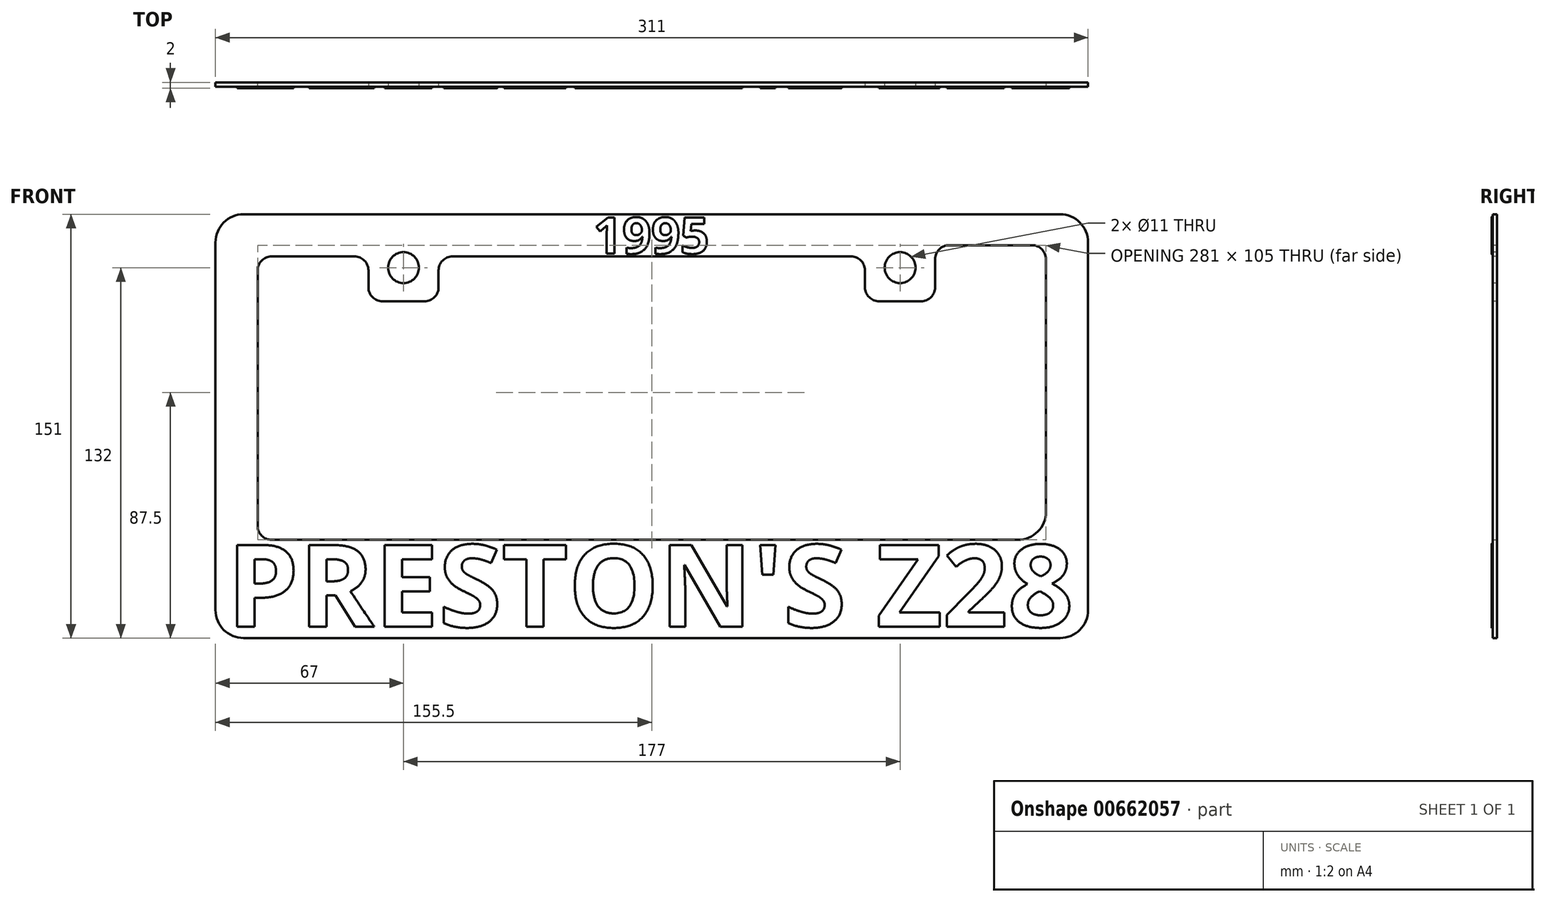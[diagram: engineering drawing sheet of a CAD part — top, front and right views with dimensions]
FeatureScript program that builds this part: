
annotation { "Feature Type Name" : "Feature", "Feature Type Description" : "" }
export const myFeature = defineFeature(function(context is Context, id is Id, definition is map)
    precondition{}
    {
        {
            var Q0;
            Q0=qCreatedBy(makeId("Front.planeOp"),FACE);
            var sketch = newSketch(context, id + "F0", { "sketchPlane" : qUnion([Q0])});
            skLineSegment(sketch, "E0.bottom", {"start": v(145.5, 75.5) * mm, "end": v(-145.5, 75.5) * mm});
            skLineSegment(sketch, "E0.top", {"start": v(145.5, -75.5) * mm, "end": v(-145.5, -75.5) * mm});
            skLineSegment(sketch, "E0.left", {"start": v(155.5, 65.5) * mm, "end": v(155.5, -65.5) * mm});
            skLineSegment(sketch, "E0.right", {"start": v(-155.5, 65.5) * mm, "end": v(-155.5, -65.5) * mm});
            skPoint(sketch, "E0.middle", {"position": v(0, 0) * mm});
            skLineSegment(sketch, "E1.bottom", {"start": v(135.5, 60.5) * mm, "end": v(-135.5, 60.5) * mm});
            skLineSegment(sketch, "E1.left", {"start": v(140.5, 55.5) * mm, "end": v(140.5, -30.5) * mm});
            skLineSegment(sketch, "E1.right", {"start": v(-140.5, 55.5) * mm, "end": v(-140.5, -35.5) * mm});
            skLineSegment(sketch, "E2", {"start": v(-135.5, -40.5) * mm, "end": v(130.5, -40.5) * mm});
            skPoint(sketch, "E3.orphan", {"position": v(140.5, -60.5) * mm});
            skPoint(sketch, "E4.orphan", {"position": v(-140.5, -60.5) * mm});
            skPoint(sketch, "E5.visualSharp", {"position": v(-155.5, 75.5) * mm});
            skArc(sketch, "E5.filletArc", {"start": v(-145.5, 75.5) * mm, "mid": v(-152.57, 72.57) * mm, "end": v(-155.5, 65.5) * mm});
            skPoint(sketch, "E6.visualSharp", {"position": v(-155.5, -75.5) * mm});
            skArc(sketch, "E6.filletArc", {"start": v(-155.5, -65.5) * mm, "mid": v(-152.57, -72.57) * mm, "end": v(-145.5, -75.5) * mm});
            skPoint(sketch, "E7.visualSharp", {"position": v(155.5, 75.5) * mm});
            skArc(sketch, "E7.filletArc", {"start": v(155.5, 65.5) * mm, "mid": v(152.57, 72.57) * mm, "end": v(145.5, 75.5) * mm});
            skPoint(sketch, "E8.visualSharp", {"position": v(155.5, -75.5) * mm});
            skArc(sketch, "E8.filletArc", {"start": v(145.5, -75.5) * mm, "mid": v(152.57, -72.57) * mm, "end": v(155.5, -65.5) * mm});
            skPoint(sketch, "E9.visualSharp", {"position": v(-140.5, 60.5) * mm});
            skArc(sketch, "E9.filletArc", {"start": v(-135.5, 60.5) * mm, "mid": v(-139.04, 59.04) * mm, "end": v(-140.5, 55.5) * mm});
            skPoint(sketch, "E10.visualSharp", {"position": v(-140.5, -40.5) * mm});
            skArc(sketch, "E10.filletArc", {"start": v(-140.5, -35.5) * mm, "mid": v(-139.04, -39.04) * mm, "end": v(-135.5, -40.5) * mm});
            skPoint(sketch, "E11.visualSharp", {"position": v(140.5, -40.5) * mm});
            skArc(sketch, "E11.filletArc", {"start": v(130.5, -40.5) * mm, "mid": v(137.57, -37.57) * mm, "end": v(140.5, -30.5) * mm});
            skPoint(sketch, "E12.visualSharp", {"position": v(140.5, 60.5) * mm});
            skArc(sketch, "E12.filletArc", {"start": v(140.5, 55.5) * mm, "mid": v(139.04, 59.04) * mm, "end": v(135.5, 60.5) * mm});
            skSolve(sketch);
        }
        {
            var Q0;
            Q0=qSketchRegion(id+"F0",true);
            extrude(context, id + "F1", {"entities" : qUnion([Q0]), "depth" : 1.6 * mm, "offsetDistance" : 25 * mm});
        }
        {
            var Q0;
            Q0=makeQuery(id+"F1.opExtrude","CAP_FACE",FACE,{"disambiguationData":[OSD([sQuery(id+"F0.wireOp",EDGE,"E0.bottom"),sQuery(id+"F0.wireOp",EDGE,"E0.top"),sQuery(id+"F0.wireOp",EDGE,"E0.left"),sQuery(id+"F0.wireOp",EDGE,"E0.right"),sQuery(id+"F0.wireOp",EDGE,"E1.bottom"),sQuery(id+"F0.wireOp",EDGE,"E1.left"),sQuery(id+"F0.wireOp",EDGE,"E1.right"),sQuery(id+"F0.wireOp",EDGE,"E2"),sQuery(id+"F0.wireOp",EDGE,"E5.filletArc"),sQuery(id+"F0.wireOp",EDGE,"E6.filletArc"),sQuery(id+"F0.wireOp",EDGE,"E7.filletArc"),sQuery(id+"F0.wireOp",EDGE,"E8.filletArc"),sQuery(id+"F0.wireOp",EDGE,"E9.filletArc"),sQuery(id+"F0.wireOp",EDGE,"E10.filletArc"),sQuery(id+"F0.wireOp",EDGE,"E11.filletArc"),sQuery(id+"F0.wireOp",EDGE,"E12.filletArc")])],"isStart":false});
            var sketch = newSketch(context, id + "F2", { "sketchPlane" : qUnion([Q0])});
            skLineSegment(sketch, "E13.bottom", {"start": v(-101, 60.5) * mm, "end": v(-76, 60.5) * mm});
            skLineSegment(sketch, "E13.top", {"start": v(-101, 44.5) * mm, "end": v(-76, 44.5) * mm});
            skLineSegment(sketch, "E13.left", {"start": v(-101, 60.5) * mm, "end": v(-101, 44.5) * mm});
            skLineSegment(sketch, "E13.right", {"start": v(-76, 60.5) * mm, "end": v(-76, 44.5) * mm});
            skLineSegment(sketch, "E14.bottom", {"start": v(76, 60.5) * mm, "end": v(101, 60.5) * mm});
            skLineSegment(sketch, "E14.top", {"start": v(76, 44.5) * mm, "end": v(101, 44.5) * mm});
            skLineSegment(sketch, "E14.left", {"start": v(76, 60.5) * mm, "end": v(76, 44.5) * mm});
            skLineSegment(sketch, "E14.right", {"start": v(101, 60.5) * mm, "end": v(101, 44.5) * mm});
            skLineSegment(sketch, "E15", {"start": v(-88.5, 44.5) * mm, "end": v(-88.5, 60.5) * mm, "construction": true});
            skLineSegment(sketch, "E16", {"start": v(-101, 44.5) * mm, "end": v(-140.5, 44.5) * mm, "construction": true});
            skLineSegment(sketch, "E17", {"start": v(101, 44.5) * mm, "end": v(140.5, 44.5) * mm, "construction": true});
            skSolve(sketch);
        }
        {
            var Q0;
            Q0=qSketchRegion(id+"F2",true);
            var Q1;
            Q1=makeQuery(id+"F1.opExtrude","CAP_FACE",FACE,{"disambiguationData":[OSD([sQuery(id+"F0.wireOp",EDGE,"E0.bottom"),sQuery(id+"F0.wireOp",EDGE,"E0.top"),sQuery(id+"F0.wireOp",EDGE,"E0.left"),sQuery(id+"F0.wireOp",EDGE,"E0.right"),sQuery(id+"F0.wireOp",EDGE,"E1.bottom"),sQuery(id+"F0.wireOp",EDGE,"E1.left"),sQuery(id+"F0.wireOp",EDGE,"E1.right"),sQuery(id+"F0.wireOp",EDGE,"E2"),sQuery(id+"F0.wireOp",EDGE,"E5.filletArc"),sQuery(id+"F0.wireOp",EDGE,"E6.filletArc"),sQuery(id+"F0.wireOp",EDGE,"E7.filletArc"),sQuery(id+"F0.wireOp",EDGE,"E8.filletArc"),sQuery(id+"F0.wireOp",EDGE,"E9.filletArc"),sQuery(id+"F0.wireOp",EDGE,"E10.filletArc"),sQuery(id+"F0.wireOp",EDGE,"E11.filletArc"),sQuery(id+"F0.wireOp",EDGE,"E12.filletArc")])],"isStart":true});
            extrude(context, id + "F3", {"entities" : qUnion([Q0]), "operationType" : NewBodyOperationType.ADD, "endBound" : BoundingType.UP_TO_SURFACE, "oppositeDirection" : true, "endBoundEntityFace" : qUnion([Q1]), "depth" : 25 * mm});
        }
        {
            var Q0;
            Q0=makeQuery(id+"F3.boolean.opBoolean","MERGE",FACE,{"derivedFrom":[makeQuery(id+"F1.opExtrude","CAP_FACE",FACE,{"disambiguationData":[OSD([sQuery(id+"F0.wireOp",EDGE,"E0.bottom"),sQuery(id+"F0.wireOp",EDGE,"E0.top"),sQuery(id+"F0.wireOp",EDGE,"E0.left"),sQuery(id+"F0.wireOp",EDGE,"E0.right"),sQuery(id+"F0.wireOp",EDGE,"E1.bottom"),sQuery(id+"F0.wireOp",EDGE,"E1.left"),sQuery(id+"F0.wireOp",EDGE,"E1.right"),sQuery(id+"F0.wireOp",EDGE,"E2"),sQuery(id+"F0.wireOp",EDGE,"E5.filletArc"),sQuery(id+"F0.wireOp",EDGE,"E6.filletArc"),sQuery(id+"F0.wireOp",EDGE,"E7.filletArc"),sQuery(id+"F0.wireOp",EDGE,"E8.filletArc"),sQuery(id+"F0.wireOp",EDGE,"E9.filletArc"),sQuery(id+"F0.wireOp",EDGE,"E10.filletArc"),sQuery(id+"F0.wireOp",EDGE,"E11.filletArc"),sQuery(id+"F0.wireOp",EDGE,"E12.filletArc")])],"isStart":false}),makeQuery(id+"F3.opExtrude","CAP_FACE",FACE,{"disambiguationData":[OSD([sQuery(id+"F2.wireOp",EDGE,"E13.bottom"),sQuery(id+"F2.wireOp",EDGE,"E13.top"),sQuery(id+"F2.wireOp",EDGE,"E13.left"),sQuery(id+"F2.wireOp",EDGE,"E13.right")])],"isStart":true}),makeQuery(id+"F3.opExtrude","CAP_FACE",FACE,{"disambiguationData":[OSD([sQuery(id+"F2.wireOp",EDGE,"E14.bottom"),sQuery(id+"F2.wireOp",EDGE,"E14.top"),sQuery(id+"F2.wireOp",EDGE,"E14.left"),sQuery(id+"F2.wireOp",EDGE,"E14.right")])],"isStart":true})]});
            var sketch = newSketch(context, id + "F4", { "sketchPlane" : qUnion([Q0])});
            skLineSegment(sketch, "E18", {"start": v(101, 60.5) * mm, "end": v(101, 64.5) * mm});
            skLineSegment(sketch, "E19", {"start": v(101, 64.5) * mm, "end": v(140.5, 64.5) * mm});
            skLineSegment(sketch, "E20", {"start": v(140.5, 55.5) * mm, "end": v(101, 55.5) * mm});
            skLineSegment(sketch, "E21", {"start": v(140.5, 55.5) * mm, "end": v(140.5, 64.5) * mm});
            skLineSegment(sketch, "E22", {"start": v(101, 60.5) * mm, "end": v(101, 55.5) * mm});
            skSolve(sketch);
        }
        {
            var Q0;
            Q0=qSketchRegion(id+"F4",true);
            extrude(context, id + "F5", {"entities" : qUnion([Q0]), "operationType" : NewBodyOperationType.REMOVE, "oppositeDirection" : true, "depth" : 25 * mm});
        }
        {
            var Q0;
            Q0=makeQuery(id+"F3.opExtrude","SWEPT_EDGE",EDGE,{"disambiguationData":[OSD([sQuery(id+"F2.wireOp",EDGE,"E13.top"),sQuery(id+"F2.wireOp",EDGE,"E13.left")])]});
            var Q1;
            Q1=makeQuery(id+"F3.opExtrude","SWEPT_EDGE",EDGE,{"disambiguationData":[OSD([sQuery(id+"F0.wireOp",EDGE,"E1.bottom"),sQuery(id+"F2.wireOp",EDGE,"E13.bottom"),sQuery(id+"F2.wireOp",EDGE,"E13.left")])]});
            var Q2;
            Q2=makeQuery(id+"F3.opExtrude","SWEPT_EDGE",EDGE,{"disambiguationData":[OSD([sQuery(id+"F2.wireOp",EDGE,"E13.top"),sQuery(id+"F2.wireOp",EDGE,"E13.right")])]});
            var Q3;
            Q3=makeQuery(id+"F3.opExtrude","SWEPT_EDGE",EDGE,{"disambiguationData":[OSD([sQuery(id+"F0.wireOp",EDGE,"E1.bottom"),sQuery(id+"F2.wireOp",EDGE,"E13.bottom"),sQuery(id+"F2.wireOp",EDGE,"E13.right")])]});
            var Q4;
            Q4=makeQuery(id+"F3.opExtrude","SWEPT_EDGE",EDGE,{"disambiguationData":[OSD([sQuery(id+"F2.wireOp",EDGE,"E14.top"),sQuery(id+"F2.wireOp",EDGE,"E14.right")])]});
            var Q5;
            Q5=makeQuery(id+"F3.opExtrude","SWEPT_EDGE",EDGE,{"disambiguationData":[OSD([sQuery(id+"F0.wireOp",EDGE,"E1.bottom"),sQuery(id+"F2.wireOp",EDGE,"E14.bottom"),sQuery(id+"F2.wireOp",EDGE,"E14.right")])]});
            var Q6;
            Q6=makeQuery(id+"F3.opExtrude","SWEPT_EDGE",EDGE,{"disambiguationData":[OSD([sQuery(id+"F2.wireOp",EDGE,"E14.top"),sQuery(id+"F2.wireOp",EDGE,"E14.left")])]});
            var Q7;
            Q7=makeQuery(id+"F3.opExtrude","SWEPT_EDGE",EDGE,{"disambiguationData":[OSD([sQuery(id+"F0.wireOp",EDGE,"E1.bottom"),sQuery(id+"F2.wireOp",EDGE,"E14.bottom"),sQuery(id+"F2.wireOp",EDGE,"E14.left")])]});
            var Q8;
            Q8=makeQuery(id+"F5.boolean.opBoolean","COPY",EDGE,{"derivedFrom":makeQuery(id+"F5.opExtrude","SWEPT_EDGE",EDGE,{"disambiguationData":[OSD([sQuery(id+"F4.wireOp",EDGE,"E19"),sQuery(id+"F4.wireOp",EDGE,"E21")])]})});
            fillet(context, id + "F6", {"entities" : qUnion([Q0, Q1, Q2, Q3, Q4, Q5, Q6, Q7, Q8]), "radius" : 5 * mm, "tangentPropagation" : true, "allowEdgeOverflow" : false});
        }
        {
            var Q0;
            Q0=makeQuery(id+"F5.boolean.opBoolean","COPY",EDGE,{"derivedFrom":makeQuery(id+"F5.opExtrude","SWEPT_EDGE",EDGE,{"disambiguationData":[OSD([sQuery(id+"F4.wireOp",EDGE,"7OP9Tv27-VSEW-8zX2-RoHM-HqM2cPaEEPGh"),sQuery(id+"F4.wireOp",EDGE,"E18")])]})});
            var Q1;
            Q1=makeQuery(id+"F5.boolean.opBoolean","COPY",EDGE,{"derivedFrom":makeQuery(id+"F5.opExtrude","SWEPT_EDGE",EDGE,{"disambiguationData":[OSD([sQuery(id+"F4.wireOp",EDGE,"aboeoGEW-dTeu-87r4-9ffM-jYBHCW7SDUxB"),sQuery(id+"F4.wireOp",EDGE,"7OP9Tv27-VSEW-8zX2-RoHM-HqM2cPaEEPGh")])]})});
            fillet(context, id + "F7", {"entities" : qUnion([Q0, Q1]), "radius" : 5 * mm, "tangentPropagation" : true, "allowEdgeOverflow" : false});
        }
        {
            var Q0;
            Q0=makeQuery(id+"F3.boolean.opBoolean","MERGE",FACE,{"derivedFrom":[makeQuery(id+"F1.opExtrude","CAP_FACE",FACE,{"disambiguationData":[OSD([sQuery(id+"F0.wireOp",EDGE,"E0.bottom"),sQuery(id+"F0.wireOp",EDGE,"E0.top"),sQuery(id+"F0.wireOp",EDGE,"E0.left"),sQuery(id+"F0.wireOp",EDGE,"E0.right"),sQuery(id+"F0.wireOp",EDGE,"E1.bottom"),sQuery(id+"F0.wireOp",EDGE,"E1.left"),sQuery(id+"F0.wireOp",EDGE,"E1.right"),sQuery(id+"F0.wireOp",EDGE,"E2"),sQuery(id+"F0.wireOp",EDGE,"E5.filletArc"),sQuery(id+"F0.wireOp",EDGE,"E6.filletArc"),sQuery(id+"F0.wireOp",EDGE,"E7.filletArc"),sQuery(id+"F0.wireOp",EDGE,"E8.filletArc"),sQuery(id+"F0.wireOp",EDGE,"E9.filletArc"),sQuery(id+"F0.wireOp",EDGE,"E10.filletArc"),sQuery(id+"F0.wireOp",EDGE,"E11.filletArc"),sQuery(id+"F0.wireOp",EDGE,"E12.filletArc")])],"isStart":false}),makeQuery(id+"F3.opExtrude","CAP_FACE",FACE,{"disambiguationData":[OSD([sQuery(id+"F2.wireOp",EDGE,"E13.bottom"),sQuery(id+"F2.wireOp",EDGE,"E13.top"),sQuery(id+"F2.wireOp",EDGE,"E13.left"),sQuery(id+"F2.wireOp",EDGE,"E13.right")])],"isStart":true}),makeQuery(id+"F3.opExtrude","CAP_FACE",FACE,{"disambiguationData":[OSD([sQuery(id+"F2.wireOp",EDGE,"E14.bottom"),sQuery(id+"F2.wireOp",EDGE,"E14.top"),sQuery(id+"F2.wireOp",EDGE,"E14.left"),sQuery(id+"F2.wireOp",EDGE,"E14.right")])],"isStart":true})]});
            var sketch = newSketch(context, id + "F8", { "sketchPlane" : qUnion([Q0])});
            skCircle(sketch, "E23", {"center": v(-88.5, 56.5) * mm, "radius": 5.5 * mm});
            skCircle(sketch, "E24", {"center": v(88.5, 56.5) * mm, "radius": 5.5 * mm});
            skLineSegment(sketch, "E25", {"start": v(-88.5, 44.5) * mm, "end": v(-88.5, 89.98) * mm, "construction": true});
            skLineSegment(sketch, "E26", {"start": v(88.5, 44.5) * mm, "end": v(88.5, 67.92) * mm, "construction": true});
            skSolve(sketch);
        }
        {
            var Q0;
            Q0=qSketchRegion(id+"F8",true);
            extrude(context, id + "F9", {"entities" : qUnion([Q0]), "operationType" : NewBodyOperationType.REMOVE, "oppositeDirection" : true, "depth" : 25 * mm});
        }
        {
            var Q0;
            Q0=makeQuery(id+"F3.boolean.opBoolean","MERGE",FACE,{"derivedFrom":[makeQuery(id+"F1.opExtrude","CAP_FACE",FACE,{"disambiguationData":[OSD([sQuery(id+"F0.wireOp",EDGE,"E0.bottom"),sQuery(id+"F0.wireOp",EDGE,"E0.top"),sQuery(id+"F0.wireOp",EDGE,"E0.left"),sQuery(id+"F0.wireOp",EDGE,"E0.right"),sQuery(id+"F0.wireOp",EDGE,"E1.bottom"),sQuery(id+"F0.wireOp",EDGE,"E1.left"),sQuery(id+"F0.wireOp",EDGE,"E1.right"),sQuery(id+"F0.wireOp",EDGE,"E2"),sQuery(id+"F0.wireOp",EDGE,"E5.filletArc"),sQuery(id+"F0.wireOp",EDGE,"E6.filletArc"),sQuery(id+"F0.wireOp",EDGE,"E7.filletArc"),sQuery(id+"F0.wireOp",EDGE,"E8.filletArc"),sQuery(id+"F0.wireOp",EDGE,"E9.filletArc"),sQuery(id+"F0.wireOp",EDGE,"E10.filletArc"),sQuery(id+"F0.wireOp",EDGE,"E11.filletArc"),sQuery(id+"F0.wireOp",EDGE,"E12.filletArc")])],"isStart":false}),makeQuery(id+"F3.opExtrude","CAP_FACE",FACE,{"disambiguationData":[OSD([sQuery(id+"F2.wireOp",EDGE,"E13.bottom"),sQuery(id+"F2.wireOp",EDGE,"E13.top"),sQuery(id+"F2.wireOp",EDGE,"E13.left"),sQuery(id+"F2.wireOp",EDGE,"E13.right")])],"isStart":true}),makeQuery(id+"F3.opExtrude","CAP_FACE",FACE,{"disambiguationData":[OSD([sQuery(id+"F2.wireOp",EDGE,"E14.bottom"),sQuery(id+"F2.wireOp",EDGE,"E14.top"),sQuery(id+"F2.wireOp",EDGE,"E14.left"),sQuery(id+"F2.wireOp",EDGE,"E14.right")])],"isStart":true})]});
            var sketch = newSketch(context, id + "F10", { "sketchPlane" : qUnion([Q0])});
            skText(sketch, "E27", { "text": "1995", "fontName": "OpenSans-Bold.ttf"});
            const initialGuessF10  = {"E27": [-0.0208, 0.0615, 1, 0, 0.013]};
            skSetInitialGuess(sketch, initialGuessF10);
            skSolve(sketch);
        }
        {
            var Q0;
            Q0=qSketchRegion(id+"F10",true);
            extrude(context, id + "F11", {"entities" : qUnion([Q0]), "operationType" : NewBodyOperationType.ADD, "depth" : .4 * mm});
        }
        {
            var Q0;
            {var subQ0=sQuery(id+"F0.wireOp",EDGE,"E0.right");var subQ2=sQuery(id+"F2.wireOp",EDGE,"E14.left");var subQ3=sQuery(id+"F2.wireOp",EDGE,"E14.bottom");var subQ4=sQuery(id+"F0.wireOp",EDGE,"E1.bottom");var subQ5=sQuery(id+"F2.wireOp",EDGE,"E14.right");var subQ6=sQuery(id+"F2.wireOp",EDGE,"E14.top");var subQ7=sQuery(id+"F0.wireOp",EDGE,"E8.filletArc");var subQ8=sQuery(id+"F0.wireOp",EDGE,"E5.filletArc");var subQ9=sQuery(id+"F0.wireOp",EDGE,"E7.filletArc");var subQ10=sQuery(id+"F0.wireOp",EDGE,"E2");var subQ11=sQuery(id+"F0.wireOp",EDGE,"E6.filletArc");var subQ12=sQuery(id+"F0.wireOp",EDGE,"E1.right");var subQ13=sQuery(id+"F2.wireOp",EDGE,"E13.right");var subQ14=sQuery(id+"F2.wireOp",EDGE,"E13.top");var subQ15=sQuery(id+"F0.wireOp",EDGE,"E1.left");var subQ16=sQuery(id+"F0.wireOp",EDGE,"E9.filletArc");var subQ17=sQuery(id+"F2.wireOp",EDGE,"E13.bottom");var subQ18=sQuery(id+"F0.wireOp",EDGE,"E0.bottom");var subQ19=sQuery(id+"F0.wireOp",EDGE,"E0.top");var subQ20=sQuery(id+"F0.wireOp",EDGE,"E0.left");var subQ21=sQuery(id+"F0.wireOp",EDGE,"E10.filletArc");var subQ23=sQuery(id+"F2.wireOp",EDGE,"E13.left");var subQ24=sQuery(id+"F0.wireOp",EDGE,"E11.filletArc");Q0=makeQuery(id+"F11.boolean.opBoolean","SPLIT",FACE,{"disambiguationData":[TD([makeQuery(id+"F1.opExtrude","SWEPT_FACE",FACE,{"disambiguationData":[OSD([subQ18])]})])],"derivedFrom":makeQuery(id+"F3.boolean.opBoolean","MERGE",FACE,{"derivedFrom":[makeQuery(id+"F1.opExtrude","CAP_FACE",FACE,{"disambiguationData":[OSD([subQ18,subQ19,subQ20,subQ0,subQ4,subQ15,subQ12,subQ10,subQ8,subQ11,subQ9,subQ7,subQ16,subQ21,subQ24,sQuery(id+"F0.wireOp",EDGE,"E12.filletArc")])],"isStart":false}),makeQuery(id+"F3.opExtrude","CAP_FACE",FACE,{"disambiguationData":[OSD([subQ17,subQ14,subQ23,subQ13])],"isStart":true}),makeQuery(id+"F3.opExtrude","CAP_FACE",FACE,{"disambiguationData":[OSD([subQ3,subQ6,subQ2,subQ5])],"isStart":true})]})});}
            var sketch = newSketch(context, id + "F12", { "sketchPlane" : qUnion([Q0])});
            skText(sketch, "E28", { "text": "PRESTON\'S Z28", "fontName": "OpenSans-Bold.ttf"});
            const initialGuessF12  = {"E28": [-0.1515, -0.0715, 1, 0, 0.02942]};
            skSetInitialGuess(sketch, initialGuessF12);
            skSolve(sketch);
        }
        {
            var Q0;
            Q0=qSketchRegion(id+"F12",true);
            extrude(context, id + "F13", {"entities" : qUnion([Q0]), "operationType" : NewBodyOperationType.ADD, "depth" : .4 * mm});
        }
    });
